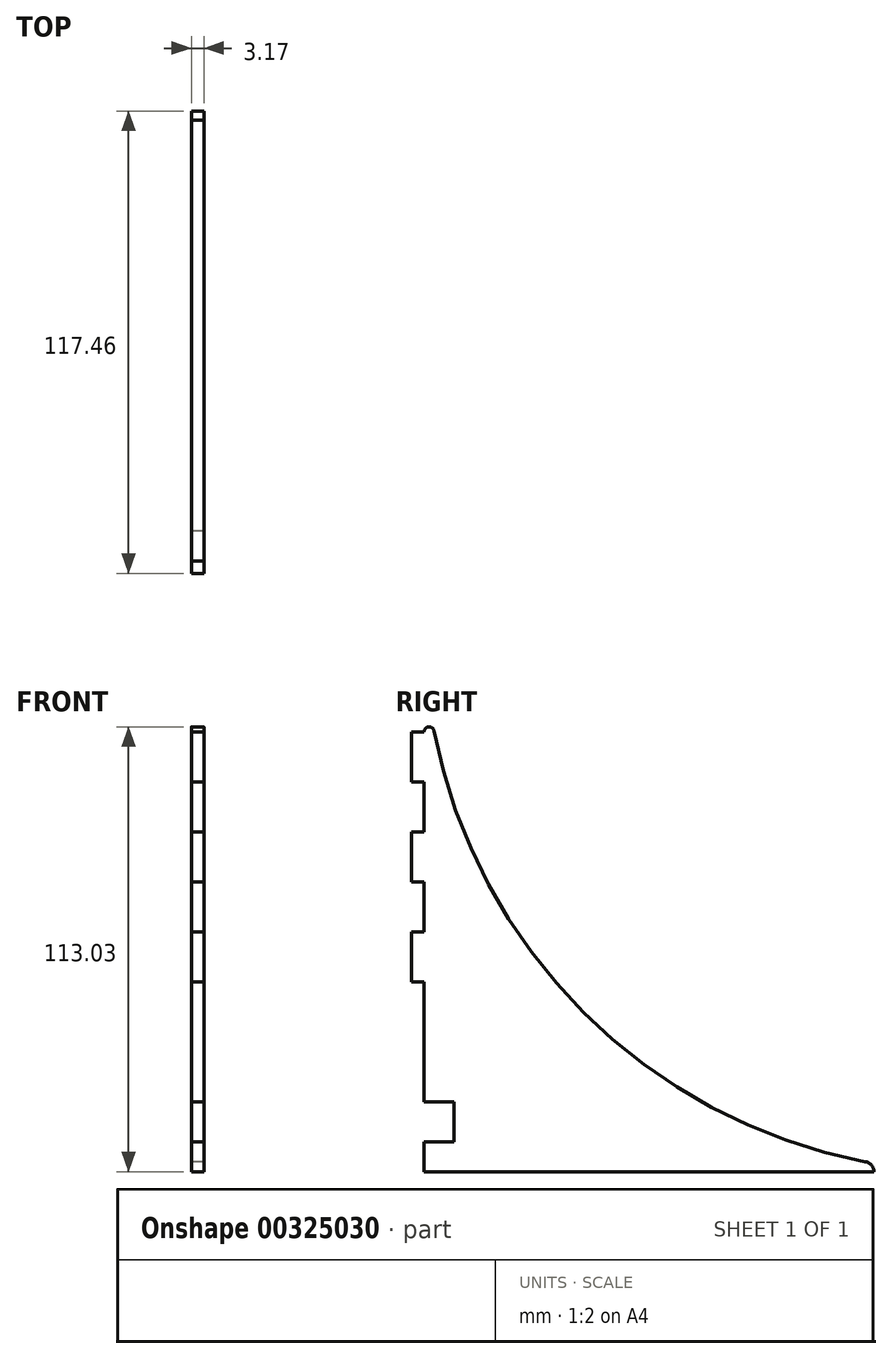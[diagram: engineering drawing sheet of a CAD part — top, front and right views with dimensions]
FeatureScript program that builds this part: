
annotation { "Feature Type Name" : "Feature", "Feature Type Description" : "" }
export const myFeature = defineFeature(function(context is Context, id is Id, definition is map)
    precondition{}
    {
        {
            var Q0;
            Q0=qCreatedBy(makeId("Right.planeOp"),FACE);
            var sketch = newSketch(context, id + "F0", { "sketchPlane" : qUnion([Q0])});
            skLineSegment(sketch, "E0", {"start": v(-48.46, 38.1) * mm, "end": v(-48.46, -73.66) * mm});
            skLineSegment(sketch, "E1", {"start": v(-48.46, -73.66) * mm, "end": v(63.3, -73.66) * mm});
            skArc(sketch, "E2", {"start": v(-45.94, 38.34) * mm, "mid": v(-7.96, -33.16) * mm, "end": v(63.54, -71.14) * mm});
            skPoint(sketch, "E3.visualSharp", {"position": v(89.8, -73.66) * mm});
            skPoint(sketch, "E4.visualSharp", {"position": v(-48.46, 64.6) * mm});
            skArc(sketch, "E4.filletArc", {"start": v(-45.94, 38.34) * mm, "mid": v(-47.3, 39.36) * mm, "end": v(-48.46, 38.1) * mm});
            skLineSegment(sketch, "E5", {"start": v(-48.46, 38.1) * mm, "end": v(-51.63, 38.1) * mm});
            skLineSegment(sketch, "E6", {"start": v(-51.63, 38.1) * mm, "end": v(-51.63, 25.4) * mm});
            skLineSegment(sketch, "E7", {"start": v(-51.63, 25.4) * mm, "end": v(-48.46, 25.4) * mm});
            skLineSegment(sketch, "E8", {"start": v(-48.46, 12.7) * mm, "end": v(-51.63, 12.7) * mm});
            skLineSegment(sketch, "E9", {"start": v(-51.63, 12.7) * mm, "end": v(-51.63, 0) * mm});
            skLineSegment(sketch, "E10", {"start": v(-51.63, 0) * mm, "end": v(-48.46, 0) * mm});
            skLineSegment(sketch, "E11", {"start": v(-48.46, -12.7) * mm, "end": v(-51.63, -12.7) * mm});
            skLineSegment(sketch, "E12", {"start": v(-51.63, -12.7) * mm, "end": v(-51.63, -25.4) * mm});
            skLineSegment(sketch, "E13", {"start": v(-51.63, -25.4) * mm, "end": v(-48.46, -25.4) * mm});
            skLineSegment(sketch, "E14", {"start": v(-51.63, 25.4) * mm, "end": v(-51.63, 12.7) * mm, "construction": true});
            skLineSegment(sketch, "E15", {"start": v(-51.63, 0) * mm, "end": v(-51.63, -12.7) * mm, "construction": true});
            skLineSegment(sketch, "E16.bottom", {"start": v(-48.46, -73.66) * mm, "end": v(-40.84, -73.66) * mm});
            skLineSegment(sketch, "E16.top", {"start": v(-48.46, -66.04) * mm, "end": v(-40.84, -66.04) * mm});
            skLineSegment(sketch, "E16.left", {"start": v(-48.46, -73.66) * mm, "end": v(-48.46, -66.04) * mm});
            skLineSegment(sketch, "E17", {"start": v(-40.84, -66.04) * mm, "end": v(-40.84, -55.88) * mm});
            skLineSegment(sketch, "E18", {"start": v(-40.84, -55.88) * mm, "end": v(-48.46, -55.88) * mm});
            skArc(sketch, "E19", {"start": v(63.54, -71.14) * mm, "mid": v(65.17, -71.96) * mm, "end": v(65.83, -73.66) * mm});
            skLineSegment(sketch, "E20", {"start": v(63.3, -73.66) * mm, "end": v(65.83, -73.66) * mm});
            skSolve(sketch);
        }
        {
            var Q0;
            {var subQ7=sQuery(id+"F0.wireOp",EDGE,"E1");Q0=makeQuery(id+"F0.imprint","IMPRINT",FACE,{"disambiguationData":[TD([[makeQuery(id+"F0.imprint","IMPRINT",EDGE,{"derivedFrom":subQ7}),1.0]])]});}
            var Q1;
            {var subQ0=sQuery(id+"F0.wireOp",EDGE,"E5");Q1=makeQuery(id+"F0.imprint","IMPRINT",FACE,{"disambiguationData":[TD([[makeQuery(id+"F0.imprint","IMPRINT",EDGE,{"derivedFrom":subQ0}),1.0]])]});}
            var Q2;
            {var subQ0=sQuery(id+"F0.wireOp",EDGE,"E8");Q2=makeQuery(id+"F0.imprint","IMPRINT",FACE,{"disambiguationData":[TD([[makeQuery(id+"F0.imprint","IMPRINT",EDGE,{"derivedFrom":subQ0}),1.0]])]});}
            var Q3;
            {var subQ0=sQuery(id+"F0.wireOp",EDGE,"E11");Q3=makeQuery(id+"F0.imprint","IMPRINT",FACE,{"disambiguationData":[TD([[makeQuery(id+"F0.imprint","IMPRINT",EDGE,{"derivedFrom":subQ0}),1.0]])]});}
            extrude(context, id + "F1", {"entities" : qUnion([Q0, Q1, Q2, Q3]), "depth" : 3.17 * mm});
        }
    });
